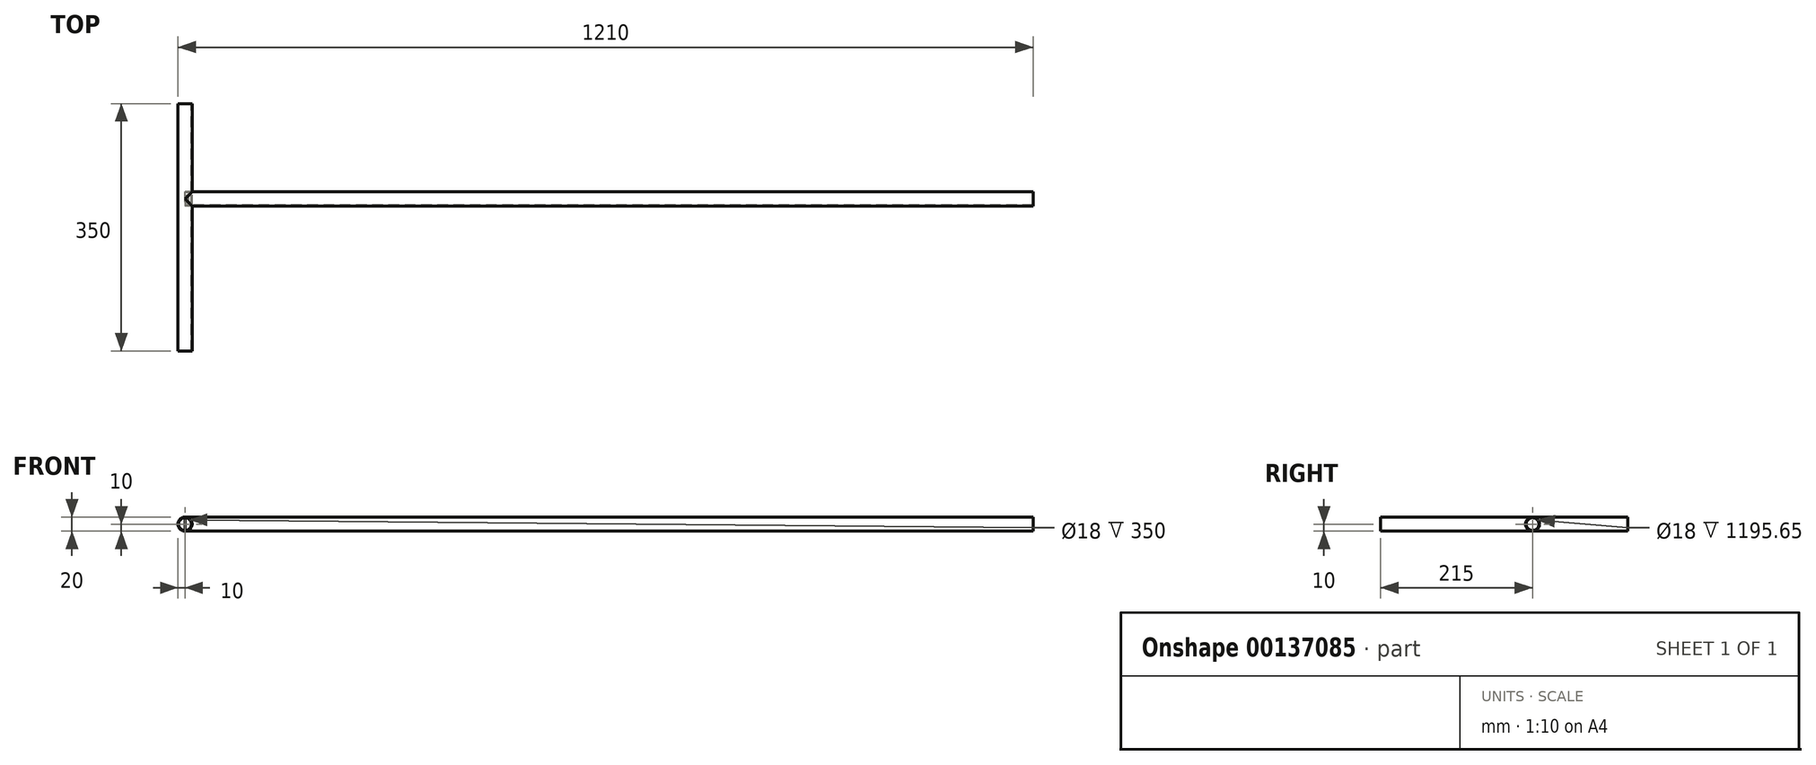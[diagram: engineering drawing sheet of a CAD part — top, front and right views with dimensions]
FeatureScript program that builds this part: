
annotation { "Feature Type Name" : "Feature", "Feature Type Description" : "" }
export const myFeature = defineFeature(function(context is Context, id is Id, definition is map)
    precondition{}
    {
        {
            var Q0;
            Q0=qCreatedBy(makeId("Right.planeOp"),FACE);
            var sketch = newSketch(context, id + "F0", { "sketchPlane" : qUnion([Q0])});
            skCircle(sketch, "E0", {"center": v(0, 0) * mm, "radius": 9 * mm});
            skCircle(sketch, "E1", {"center": v(0, 0) * mm, "radius": 10 * mm});
            skSolve(sketch);
        }
        {
            var Q0;
            Q0 = qSketchRegion(id + "F0", true);
            extrude(context, id + "F1", {"entities" : qUnion([Q0]), "endBound" : BoundingType.SYMMETRIC, "depth" : 1200 * mm});
        }
        {
            var Q0;
            Q0=qCreatedBy(makeId("Front.planeOp"),FACE);
            var sketch = newSketch(context, id + "F2", { "sketchPlane" : qUnion([Q0])});
            skLineSegment(sketch, "E2", {"start": v(0, 0) * mm, "end": v(-600, 0) * mm, "construction": true});
            skCircle(sketch, "E3", {"center": v(-600, 0) * mm, "radius": 10 * mm});
            skLineSegment(sketch, "E4", {"start": v(0, 0) * mm, "end": v(0, -62.62) * mm, "construction": true});
            skCircle(sketch, "E5.MirrorC", {"center": v(600, 0) * mm, "radius": 10 * mm});
            skCircle(sketch, "E6", {"center": v(-600, 0) * mm, "radius": 9 * mm});
            skCircle(sketch, "E7.MirrorC", {"center": v(600, 0) * mm, "radius": 9 * mm});
            skSolve(sketch);
        }
        {
            var Q0;
            Q0=makeQuery(id+"F2.imprint","IMPRINT",FACE,{"disambiguationData":[TD([[makeQuery(id+"F2.imprint","IMPRINT",EDGE,{"derivedFrom":sQuery(id+"F2.wireOp",EDGE,"E3")}),1.0]])]});
            var Q1;
            Q1=makeQuery(id+"F2.imprint","IMPRINT",FACE,{"disambiguationData":[TD([[makeQuery(id+"F2.imprint","IMPRINT",EDGE,{"derivedFrom":sQuery(id+"F2.wireOp",EDGE,"E5.MirrorC")}),-1.0]])]});
            extrude(context, id + "F3", {"entities" : qUnion([Q0, Q1]), "operationType" : NewBodyOperationType.ADD, "depth" : 215 * mm, "hasSecondDirection" : true, "secondDirectionOppositeDirection" : true, "secondDirectionDepth" : 135 * mm});
        }
    });
